# Revit family: 2NaughtOne_Mimo3-PositionModularWithTable
name_source: partatom
category: Furniture
units: mm (PartAtom-declared; Revit-internal decimal feet)

## family parameters
Always vertical = Yes
Cut with Voids When Loaded = No
OmniClass Number = 23.40.70.14.64.14
OmniClass Title = Retail and Commercial Seating Furniture
Room Calculation Point = No
Shared = No
Work Plane-Based = No

## types (1)
- Seat with Back Seat with Back Table
    Assembly Code = E2010200
    Back C = Yes
    Back L = No
    Back R = Yes
    Brand = NaughtOne
    Center Arm Left = No
    Center Arm Right = No
    Center Back = Yes
    Center Seat = Yes
    Center Table = No
    Default Elevation = 0 "
    Description = Mimo 3 Position Modular Seat with Back Seat with Back Table
    Left Back = Yes
    Left Corner = No
    Left Seat = Yes
    Left Table = No
    Manufacturer = MillerKnoll, Inc.
    Model = NOMMO3BBT
    Package Qty = 1
    Right Back = No
    Right Corner = No
    Right Seat = No
    Right Table = Yes
    Seat L = Yes
    Seat R = No
    Tag = NOMMO3BBT
    Type = 1
    Type 1 = Yes
    Type 13 = No
    Type 2 = No
    Type 3 = No
    Type 4 = No
    Type 5 = No
    Type 6 = No
    Type 7 = No
    URL = https://www.naughtone.com

## geometry (parser evidence)
native form markers: Sweep x11
no freeform markers — native parametric forms only
